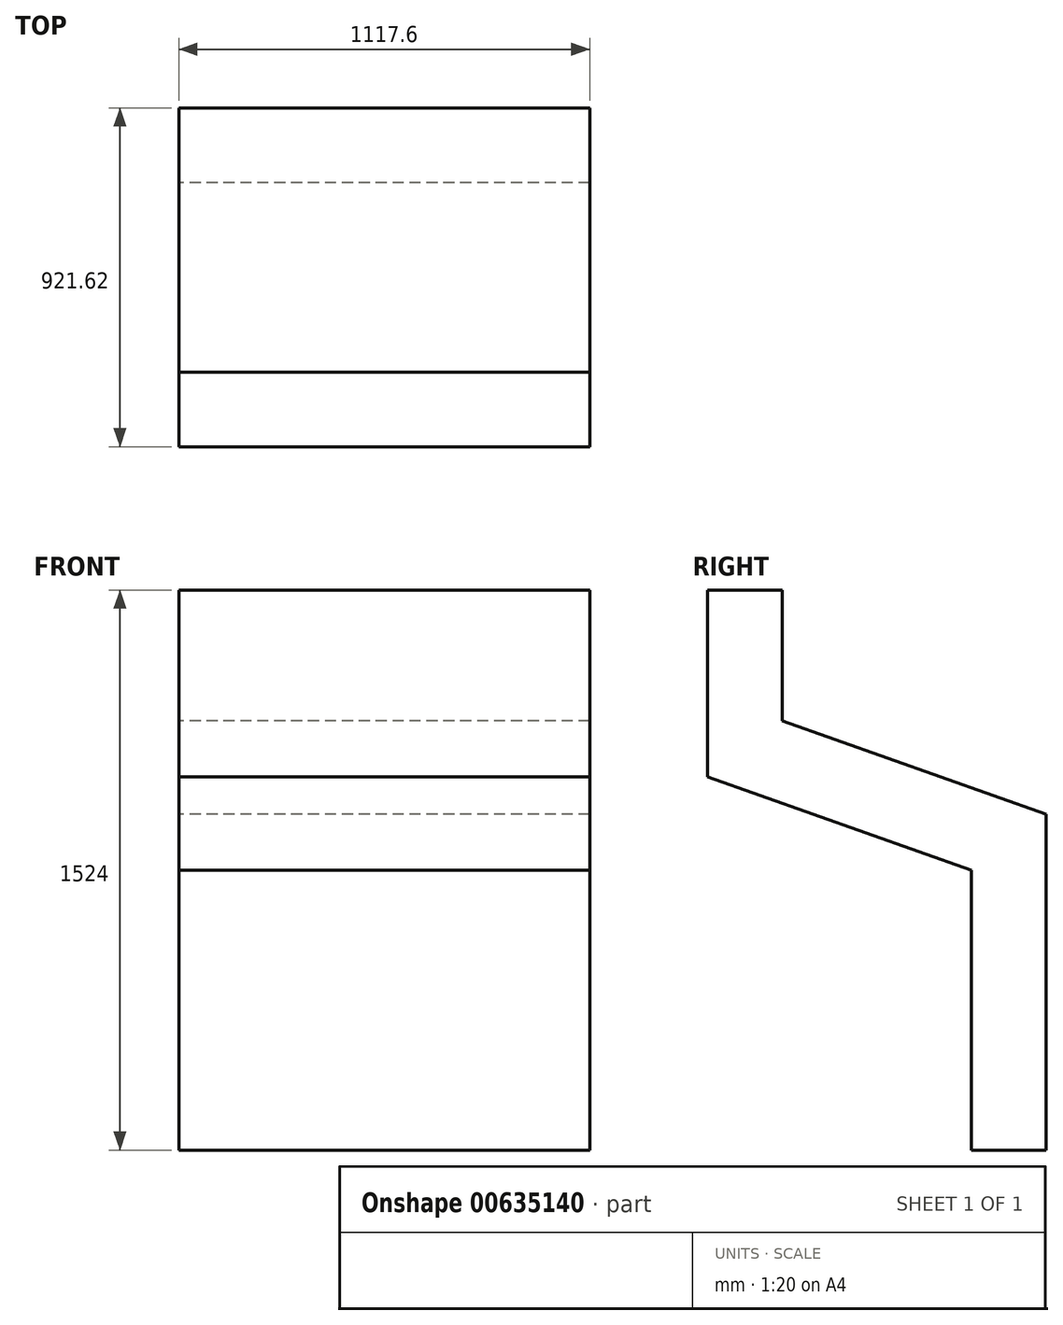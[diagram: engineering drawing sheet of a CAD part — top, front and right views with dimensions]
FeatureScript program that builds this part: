
annotation { "Feature Type Name" : "Feature", "Feature Type Description" : "" }
export const myFeature = defineFeature(function(context is Context, id is Id, definition is map)
    precondition{}
    {
        {
            var Q0;
            Q0=qCreatedBy(makeId("Right.planeOp"),FACE);
            var sketch = newSketch(context, id + "F0", { "sketchPlane" : qUnion([Q0])});
            skLineSegment(sketch, "E0", {"start": v(480.98, -879.45) * mm, "end": v(684.18, -879.45) * mm});
            skLineSegment(sketch, "E1", {"start": v(684.18, -879.45) * mm, "end": v(684.18, 34.95) * mm});
            skLineSegment(sketch, "E2", {"start": v(684.18, 34.95) * mm, "end": v(-34.24, 288.95) * mm});
            skLineSegment(sketch, "E3", {"start": v(-34.24, 288.95) * mm, "end": v(-34.24, 644.55) * mm});
            skLineSegment(sketch, "E4", {"start": v(-34.24, 644.55) * mm, "end": v(-237.44, 644.55) * mm});
            skLineSegment(sketch, "E5", {"start": v(-237.44, 644.55) * mm, "end": v(-237.44, 136.55) * mm});
            skLineSegment(sketch, "E6", {"start": v(-237.44, 136.55) * mm, "end": v(480.98, -117.45) * mm});
            skLineSegment(sketch, "E7", {"start": v(480.98, -117.45) * mm, "end": v(480.98, -879.45) * mm});
            skSolve(sketch);
        }
        {
            var Q0;
            Q0=makeQuery(id+"F0.imprint","IMPRINT",FACE,{"disambiguationData":[TD([[makeQuery(id+"F0.imprint","IMPRINT",EDGE,{"derivedFrom":sQuery(id+"F0.wireOp",EDGE,"E0")}),1.0]])]});
            extrude(context, id + "F1", {"entities" : qUnion([Q0]), "depth" : 1117.6 * mm, "offsetDistance" : 25.4 * mm});
        }
    });
